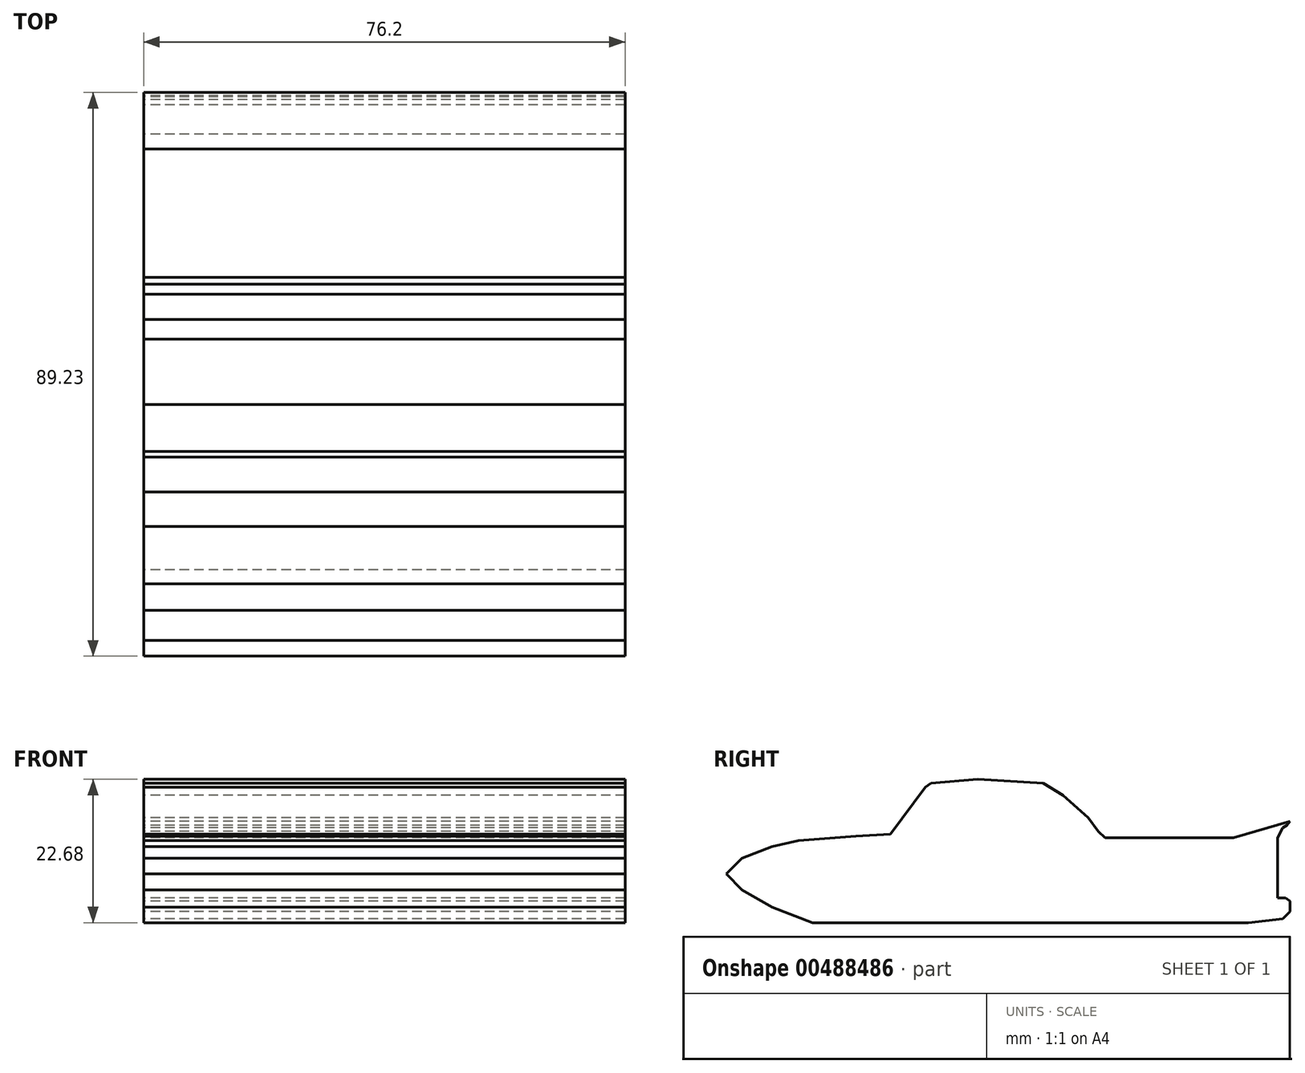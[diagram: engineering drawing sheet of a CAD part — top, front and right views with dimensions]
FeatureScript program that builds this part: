
annotation { "Feature Type Name" : "Feature", "Feature Type Description" : "" }
export const myFeature = defineFeature(function(context is Context, id is Id, definition is map)
    precondition{}
    {
        {
            var Q0;
            Q0=qCreatedBy(makeId("Right.planeOp"),FACE);
            var sketch = newSketch(context, id + "F0", { "sketchPlane" : qUnion([Q0])});
            skLineSegment(sketch, "E0", {"start": v(0, 0) * mm, "end": v(42.81, 0) * mm});
            skLineSegment(sketch, "E1", {"start": v(42.81, 0) * mm, "end": v(48.25, 0.6) * mm});
            skLineSegment(sketch, "E2", {"start": v(48.25, 0.6) * mm, "end": v(49.38, 1.72) * mm});
            skLineSegment(sketch, "E3", {"start": v(49.38, 1.72) * mm, "end": v(49.38, 3.4) * mm});
            skLineSegment(sketch, "E4", {"start": v(49.38, 3.4) * mm, "end": v(48.7, 3.89) * mm});
            skLineSegment(sketch, "E5", {"start": v(48.7, 3.89) * mm, "end": v(48.25, 3.89) * mm});
            skLineSegment(sketch, "E6", {"start": v(48.25, 3.89) * mm, "end": v(47.44, 3.89) * mm});
            skLineSegment(sketch, "E7", {"start": v(47.44, 3.89) * mm, "end": v(47.44, 5.51) * mm});
            skLineSegment(sketch, "E8", {"start": v(47.44, 5.51) * mm, "end": v(47.44, 7.6) * mm});
            skLineSegment(sketch, "E9", {"start": v(47.44, 13.44) * mm, "end": v(47.44, 7.6) * mm});
            skLineSegment(sketch, "E10", {"start": v(47.44, 13.44) * mm, "end": v(48.25, 15.02) * mm});
            skLineSegment(sketch, "E11", {"start": v(48.25, 15.02) * mm, "end": v(48.9, 15.4) * mm});
            skLineSegment(sketch, "E12", {"start": v(48.9, 15.4) * mm, "end": v(49.38, 16.05) * mm});
            skLineSegment(sketch, "E13", {"start": v(49.38, 16.05) * mm, "end": v(40.47, 13.44) * mm});
            skLineSegment(sketch, "E14", {"start": v(40.47, 13.44) * mm, "end": v(29.2, 13.44) * mm});
            skLineSegment(sketch, "E15", {"start": v(29.2, 13.44) * mm, "end": v(20.13, 13.44) * mm});
            skLineSegment(sketch, "E16", {"start": v(20.13, 13.44) * mm, "end": v(19.03, 14.47) * mm});
            skLineSegment(sketch, "E17", {"start": v(19.03, 14.47) * mm, "end": v(17.45, 16.6) * mm});
            skLineSegment(sketch, "E18", {"start": v(17.45, 16.6) * mm, "end": v(13.42, 20.15) * mm});
            skLineSegment(sketch, "E19", {"start": v(13.42, 20.15) * mm, "end": v(10.34, 22.05) * mm});
            skLineSegment(sketch, "E20", {"start": v(10.34, 22.05) * mm, "end": v(0, 22.68) * mm});
            skLineSegment(sketch, "E21", {"start": v(0, 22.68) * mm, "end": v(-7.47, 22.05) * mm});
            skLineSegment(sketch, "E22", {"start": v(-7.47, 22.05) * mm, "end": v(-8.3, 21.47) * mm});
            skLineSegment(sketch, "E23", {"start": v(-8.3, 21.47) * mm, "end": v(-13.86, 14) * mm});
            skLineSegment(sketch, "E24", {"start": v(-13.86, 14) * mm, "end": v(-19.32, 13.71) * mm});
            skLineSegment(sketch, "E25", {"start": v(-19.32, 13.71) * mm, "end": v(-28.4, 13) * mm});
            skLineSegment(sketch, "E26", {"start": v(-28.4, 13) * mm, "end": v(-32.6, 12.02) * mm});
            skLineSegment(sketch, "E27", {"start": v(-32.6, 12.02) * mm, "end": v(-37.34, 10.22) * mm});
            skLineSegment(sketch, "E28", {"start": v(-37.34, 10.22) * mm, "end": v(-39.85, 7.71) * mm});
            skLineSegment(sketch, "E29", {"start": v(-39.85, 7.71) * mm, "end": v(-37.34, 5.2) * mm});
            skLineSegment(sketch, "E30", {"start": v(-37.34, 5.2) * mm, "end": v(-32.6, 2.47) * mm});
            skLineSegment(sketch, "E31", {"start": v(-32.6, 2.47) * mm, "end": v(-26.16, 0) * mm});
            skLineSegment(sketch, "E32", {"start": v(-26.16, 0) * mm, "end": v(0, 0) * mm});
            skSolve(sketch);
        }
        {
            var Q0;
            Q0=makeQuery(id+"F0.imprint","IMPRINT",FACE,{"disambiguationData":[TD([[makeQuery(id+"F0.imprint","IMPRINT",EDGE,{"derivedFrom":sQuery(id+"F0.wireOp",EDGE,"E0")}),1.0]])]});
            extrude(context, id + "F1", {"entities" : qUnion([Q0]), "depth" : 76.2 * mm});
        }
    });
